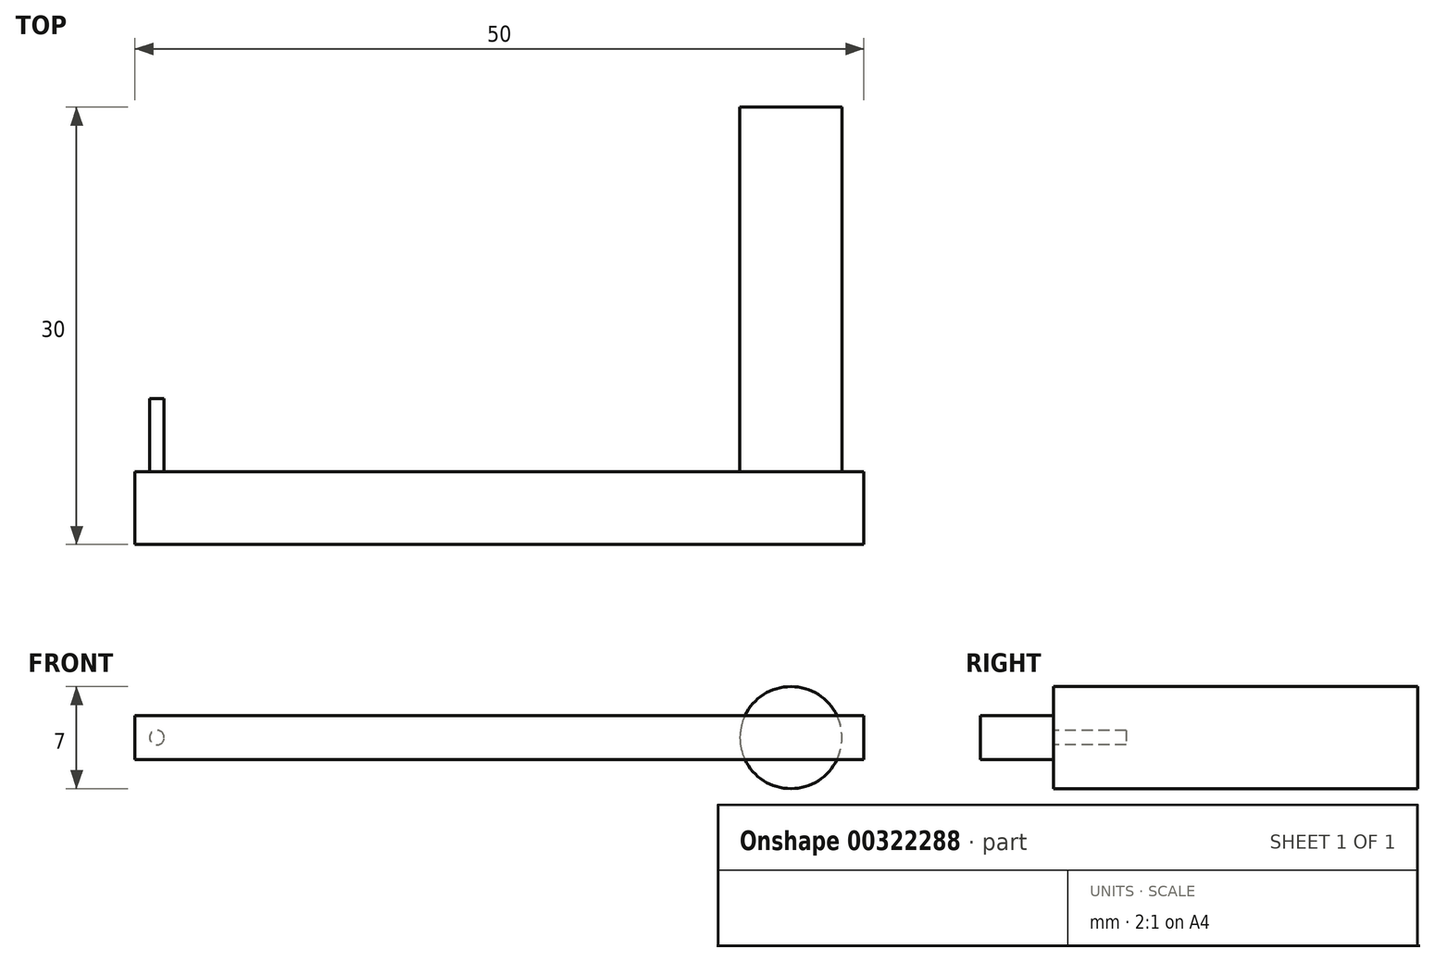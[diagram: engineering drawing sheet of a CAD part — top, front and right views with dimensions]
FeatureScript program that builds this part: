
annotation { "Feature Type Name" : "Feature", "Feature Type Description" : "" }
export const myFeature = defineFeature(function(context is Context, id is Id, definition is map)
    precondition{}
    {
        {
            var Q0;
            Q0=qCreatedBy(makeId("Top.planeOp"),FACE);
            var sketch = newSketch(context, id + "F0", { "sketchPlane" : qUnion([Q0])});
            skLineSegment(sketch, "E0.bottom", {"start": v(0, 0) * mm, "end": v(50, 0) * mm});
            skLineSegment(sketch, "E0.top", {"start": v(0, 5) * mm, "end": v(50, 5) * mm});
            skLineSegment(sketch, "E0.left", {"start": v(0, 0) * mm, "end": v(0, 5) * mm});
            skLineSegment(sketch, "E0.right", {"start": v(50, 0) * mm, "end": v(50, 5) * mm});
            skSolve(sketch);
        }
        {
            var Q0;
            Q0 = qSketchRegion(id + "F0", true);
            extrude(context, id + "F1", {"entities" : qUnion([Q0]), "depth" : 3 * mm});
        }
        {
            var Q0;
            Q0=makeQuery(id+"F1.opExtrude","SWEPT_FACE",FACE,{"disambiguationData":[OSD([sQuery(id+"F0.wireOp",EDGE,"E0.top")])]});
            var sketch = newSketch(context, id + "F2", { "sketchPlane" : qUnion([Q0])});
            skPoint(sketch, "E1", {"position": v(0, 1.5) * mm});
            skPoint(sketch, "E2", {"position": v(-1.5, 0) * mm});
            skPoint(sketch, "E3", {"position": v(0, 0) * mm});
            skPoint(sketch, "E4", {"position": v(-1.5, 1.5) * mm});
            skCircle(sketch, "E5", {"center": v(-1.5, 1.5) * mm, "radius": 0.5 * mm});
            skSolve(sketch);
        }
        {
            var Q0;
            Q0 = qSketchRegion(id + "F2", true);
            extrude(context, id + "F3", {"entities" : qUnion([Q0]), "operationType" : NewBodyOperationType.ADD, "depth" : 5 * mm});
        }
        {
            var Q0;
            Q0=makeQuery(id+"F1.opExtrude","SWEPT_FACE",FACE,{"disambiguationData":[OSD([sQuery(id+"F0.wireOp",EDGE,"E0.top")])]});
            var sketch = newSketch(context, id + "F4", { "sketchPlane" : qUnion([Q0])});
            skPoint(sketch, "E6", {"position": v(-50, 1.5) * mm});
            skPoint(sketch, "E7", {"position": v(-50, 0) * mm});
            skPoint(sketch, "E8", {"position": v(-45, 0) * mm});
            skPoint(sketch, "E9", {"position": v(-45, 1.5) * mm});
            skCircle(sketch, "E10", {"center": v(-45, 1.5) * mm, "radius": 3.5 * mm});
            skSolve(sketch);
        }
        {
            var Q0;
            Q0 = qSketchRegion(id + "F4", true);
            extrude(context, id + "F5", {"entities" : qUnion([Q0]), "operationType" : NewBodyOperationType.ADD, "depth" : 25 * mm});
        }
    });
